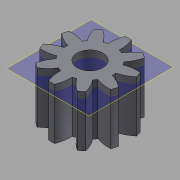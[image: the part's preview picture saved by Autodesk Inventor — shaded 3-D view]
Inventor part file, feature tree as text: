
AUTODESK INVENTOR PART (.ipt)
format: ipt  version: 2015 (Build 190159000, 159)  size: 167,424 bytes
history: native  units: in
note: dims shown in document units (in); Inventor stores cm internally (conversion verified against a paired STEP export)
features: other x13, sketch x3, plane x2
ambient origin geometry x8: Origin, YZ Plane, XZ Plane, XY Plane, X Axis, Y Axis, Z Axis, Center Point
bodies: Solid1 (feature_tree)
feature tree (18):
  other  "Spur Gear1"
  other  "Solid1::Spur Gear1"
  other  "TaggingFeature1"
  sketch  "Sketch1"  dims[d0=0.3937in]
  sketch  "Sketch2"  dims[d16=0.4528in d17=0.0in d41=0.0in d43=0.4528in d46=0.4528in d47=0.0in d48=0.0in]
  sketch  "Sketch3"
  plane  "XZ Plane_1"
  plane  "Work Plane2"
  other  "Z Axis_1"
  other  "Srf1"
  other  "Srf1::Derived"
  other  "Distance iMate"
  other  "Align iMate"
  other  "Mesh iMate"
  other  "Axis iMate"
  other  "Position iMate"
  other  "Mesh iMate2"
  other  "Start plane iMate"
